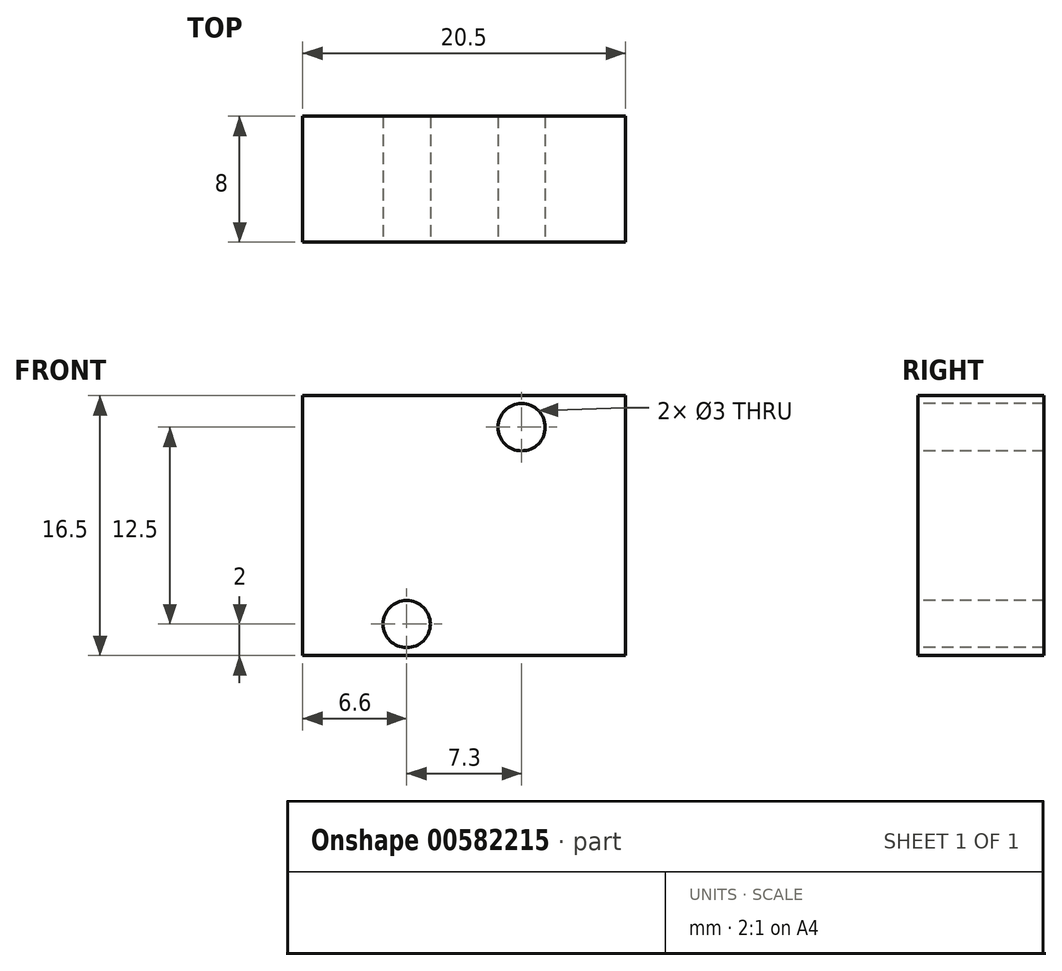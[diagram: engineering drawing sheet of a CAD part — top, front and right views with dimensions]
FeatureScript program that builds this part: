
annotation { "Feature Type Name" : "Feature", "Feature Type Description" : "" }
export const myFeature = defineFeature(function(context is Context, id is Id, definition is map)
    precondition{}
    {
        {
            var Q0;
            Q0=qCreatedBy(makeId("Front.planeOp"),FACE);
            var sketch = newSketch(context, id + "F0", { "sketchPlane" : qUnion([Q0])});
            skLineSegment(sketch, "E0.bottom", {"start": v(-10.25, 8.25) * mm, "end": v(10.25, 8.25) * mm});
            skLineSegment(sketch, "E0.top", {"start": v(-10.25, -8.25) * mm, "end": v(10.25, -8.25) * mm});
            skLineSegment(sketch, "E0.left", {"start": v(-10.25, 8.25) * mm, "end": v(-10.25, -8.25) * mm});
            skLineSegment(sketch, "E0.right", {"start": v(10.25, 8.25) * mm, "end": v(10.25, -8.25) * mm});
            skPoint(sketch, "E0.middle", {"position": v(0, 0) * mm});
            skSolve(sketch);
        }
        {
            var Q0;
            Q0=makeQuery(id+"F0.imprint","IMPRINT",FACE,{"disambiguationData":[TD([[makeQuery(id+"F0.imprint","IMPRINT",EDGE,{"derivedFrom":sQuery(id+"F0.wireOp",EDGE,"E0.bottom")}),-1.0]])]});
            extrude(context, id + "F1", {"entities" : qUnion([Q0]), "depth" : 8 * mm, "offsetDistance" : 25 * mm});
        }
        {
            var Q0;
            Q0=makeQuery(id+"F1.opExtrude","CAP_FACE",FACE,{"disambiguationData":[OSD([sQuery(id+"F0.wireOp",EDGE,"E0.bottom"),sQuery(id+"F0.wireOp",EDGE,"E0.top"),sQuery(id+"F0.wireOp",EDGE,"E0.left"),sQuery(id+"F0.wireOp",EDGE,"E0.right")])],"isStart":false});
            var sketch = newSketch(context, id + "F2", { "sketchPlane" : qUnion([Q0])});
            skCircle(sketch, "E1", {"center": v(3.65, 6.25) * mm, "radius": 1.5 * mm});
            skCircle(sketch, "E2", {"center": v(-3.65, -6.25) * mm, "radius": 1.5 * mm});
            skPoint(sketch, "E3", {"position": v(-2.15, -6.25) * mm});
            skPoint(sketch, "E4", {"position": v(2.15, 6.25) * mm});
            skSolve(sketch);
        }
        {
            var Q0;
            Q0=makeQuery(id+"F2.imprint","IMPRINT",FACE,{"disambiguationData":[TD([[makeQuery(id+"F2.imprint","IMPRINT",EDGE,{"derivedFrom":sQuery(id+"F2.wireOp",EDGE,"E1")}),1.0]])]});
            var Q1;
            Q1=makeQuery(id+"F2.imprint","IMPRINT",FACE,{"disambiguationData":[TD([[makeQuery(id+"F2.imprint","IMPRINT",EDGE,{"derivedFrom":sQuery(id+"F2.wireOp",EDGE,"E2")}),1.0]])]});
            extrude(context, id + "F3", {"entities" : qUnion([Q0, Q1]), "operationType" : NewBodyOperationType.REMOVE, "oppositeDirection" : true, "depth" : 25 * mm, "offsetDistance" : 25 * mm});
        }
        {
            var Q0;
            Q0 = qSketchRegion(id + "F2", true);
            extrude(context, id + "F4", {"entities" : qUnion([Q0]), "operationType" : NewBodyOperationType.REMOVE, "oppositeDirection" : true, "depth" : 25 * mm, "offsetDistance" : 25 * mm});
        }
        {
            var Q0;
            Q0 = qSketchRegion(id + "F2", true);
            extrude(context, id + "F5", {"entities" : qUnion([Q0]), "operationType" : NewBodyOperationType.REMOVE, "oppositeDirection" : true, "depth" : 25 * mm, "offsetDistance" : 25 * mm});
        }
    });
